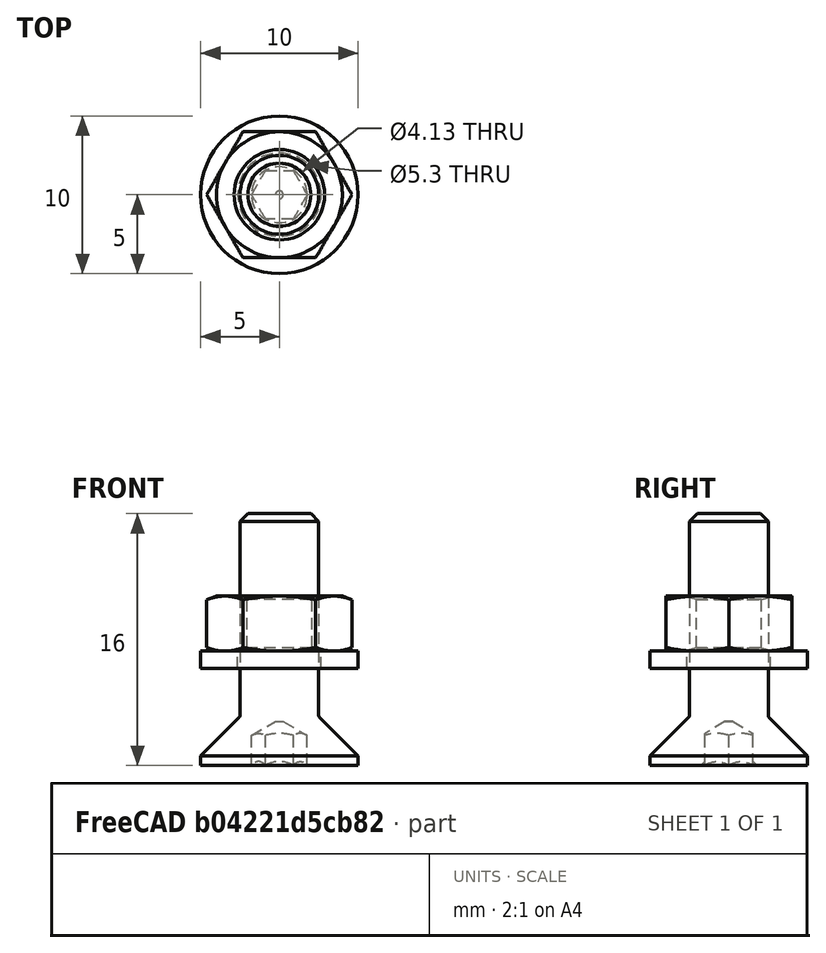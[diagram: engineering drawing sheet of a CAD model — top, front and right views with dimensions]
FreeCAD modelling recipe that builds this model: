
FCSTD DOCUMENT  (FreeCAD 0.20R29177 +426 (Git))
Label: ASM_GantrySkate
License: All rights reserved
LicenseURL: http://en.wikipedia.org/wiki/All_rights_reserved
objects: Part::FeaturePython×6, App::Link×5, App::DocumentObjectGroup×4, PartDesign::CoordinateSystem×1, App::FeaturePython×1, App::Part×1
note: 7 computed .brp shape members not serialized (recipe doc carries the construction recipe); baked Part::Feature solids carry a one-line shape summary decoded from their .brp
EXTERNAL_REF file=GantryBracket.FCStd obj=LCS_Origin
EXTERNAL_REF file=GantryBracket.FCStd obj=Assembly
EXTERNAL_REF file=GantryBracket.FCStd obj=LCS_wheel1
EXTERNAL_REF file=GantryWheel.FCStd obj=LCS_Origin
EXTERNAL_REF file=GantryWheel.FCStd obj=Assembly
EXTERNAL_REF file=GantryBracket.FCStd obj=LCS_wheel2
EXTERNAL_REF file=GantryBracket.FCStd obj=LCS_wheel3
EXTERNAL_REF file=GantryBracket.FCStd obj=LCS_wheel4
EXTERNAL_REF file=Params.FCStd obj=Spreadsheet
EXTERNAL_REF file=GantryBracket.FCStd obj=Sketch
EXTERNAL_REF file=GantryBracket.FCStd obj=Pad

FEATURE [App::DocumentObjectGroup] Parts
FEATURE [PartDesign::CoordinateSystem] LCS_Origin
  AttacherType = Attacher::AttachEngine3D
  MapMode = 2
  Support = -> [X_Axis]
FEATURE [App::FeaturePython] Variables  # WARN: FeaturePython — macro-defined, semantics opaque (R4)
  Type = App::PropertyContainer
FEATURE [App::DocumentObjectGroup] Constraints
FEATURE [App::DocumentObjectGroup] Configurations
FEATURE [App::Link] GantryBracket
  AttachedBy = #LCS_Origin
  AttachedTo = Parent Assembly#LCS_Origin
  LinkedObject = -> <external GantryBracket.FCStd>#Assembly
  SolverId = Asm4EE
  expr: Placement = LCS_Origin.Placement * AttachmentOffset * GantryBracket#LCS_Origin.Placement ^ -1
FEATURE [App::Link] GantryWheel
  AttachedBy = #LCS_Origin
  AttachedTo = GantryBracket#LCS_wheel1
  LinkPlacement = pos=(-19.85,20,3) rot=(0,0,1;1.5708rad)
  LinkedObject = -> <external GantryWheel.FCStd>#Assembly
  Placement = pos=(-19.85,20,3) rot=(0,0,1;1.5708rad)
  SolverId = Asm4EE
  expr: Placement = GantryBracket.Placement * GantryBracket#LCS_wheel1.Placement * AttachmentOffset * GantryWheel#LCS_Origin.Placement ^ -1
FEATURE [App::Link] GantryWheel001
  AttachedBy = #LCS_Origin
  AttachedTo = GantryBracket#LCS_wheel2
  LinkPlacement = pos=(19.85,20,3) rot=(0,0,1;1.5708rad)
  LinkedObject = -> <external GantryWheel.FCStd>#Assembly
  Placement = pos=(19.85,20,3) rot=(0,0,1;1.5708rad)
  SolverId = Asm4EE
  expr: Placement = GantryBracket.Placement * GantryBracket#LCS_wheel2.Placement * AttachmentOffset * GantryWheel#LCS_Origin.Placement ^ -1
FEATURE [App::Link] GantryWheel002
  AttachedBy = #LCS_Origin
  AttachedTo = GantryBracket#LCS_wheel3
  LinkPlacement = pos=(-19.85,-20,3) rot=(0,0,1;1.5708rad)
  LinkedObject = -> <external GantryWheel.FCStd>#Assembly
  Placement = pos=(-19.85,-20,3) rot=(0,0,1;1.5708rad)
  SolverId = Asm4EE
  expr: Placement = GantryBracket.Placement * GantryBracket#LCS_wheel3.Placement * AttachmentOffset * GantryWheel#LCS_Origin.Placement ^ -1
FEATURE [App::Link] GantryWheel003
  AttachedBy = #LCS_Origin
  AttachedTo = GantryBracket#LCS_wheel4
  LinkPlacement = pos=(19.85,-20,3) rot=(0,0,1;1.5708rad)
  LinkedObject = -> <external GantryWheel.FCStd>#Assembly
  Placement = pos=(19.85,-20,3) rot=(0,0,1;1.5708rad)
  SolverId = Asm4EE
  expr: Placement = GantryBracket.Placement * GantryBracket#LCS_wheel4.Placement * AttachmentOffset * GantryWheel#LCS_Origin.Placement ^ -1
FEATURE [Part::FeaturePython] Screw  label="M5x16-Screw"  # Fasteners workbench fastener (typed FeaturePython)
  Placement = pos=(19.85,0,-3.156) rot=(1,0,0;3.14159rad)
  baseObject = -> <external GantryBracket.FCStd>#Sketch [Edge23]
  diameter = 5
  invert = true
  leftHanded = false
  length = 3
  lengthCustom = 16
  matchOuter = false
  offset = 3.156
  thread = false
  type = 18
  expr: offset = <<Params>>#<<Params>>.SheetMetalThickness * 1mm + 0.5mm
FEATURE [Part::FeaturePython] Washer  label="M5-Washer"  # Fasteners workbench fastener (typed FeaturePython)
  Placement = pos=(19.85,0,3) rot=(0,0,1;0rad)
  baseObject = -> <external GantryBracket.FCStd>#Sketch [Edge23]
  diameter = 6
  invert = false
  matchOuter = false
  offset = 3
  type = 3
  expr: offset = <<GantryBracket>>#<<Pad>>.Length
FEATURE [Part::FeaturePython] Nut  label="M5-Nut"  # Fasteners workbench fastener (typed FeaturePython)
  Placement = pos=(19.85,0,4.1) rot=(0,0,1;0rad)
  baseObject = -> Washer [Edge1]
  diameter = 7
  invert = false
  leftHanded = false
  matchOuter = false
  offset = 0
  thread = false
  type = 7
FEATURE [Part::FeaturePython] Array_Screw  label="Array_M5x12-Screw"  # Draft array (typed FeaturePython)
  ArraySteps = 0
  ArrayType = Circular Array
  Axis = LCS_Origin.Z
  Count = 2
  ElementCount = 2
  FullAngle = 360
  IntervalAngle = 180
  LinearSteps = 0
  PlacementList = 2 placements: [(19.85,0,-3.156),(-19.85,2.43092e-15,-3.156)]
  ScaleList = (2) [(1,1,1),(1,1,1)]
  ShowElement = false
  SourceObject = -> Screw
FEATURE [Part::FeaturePython] Array_Washer  label="Array_M5-Washer"  # Draft array (typed FeaturePython)
  ArraySteps = 0
  ArrayType = Circular Array
  Axis = LCS_Origin.Z
  Count = 2
  ElementCount = 2
  FullAngle = 360
  IntervalAngle = 180
  LinearSteps = 0
  PlacementList = 2 placements: [(19.85,0,3),(-19.85,2.43092e-15,3)]
  ScaleList = (2) [(1,1,1),(1,1,1)]
  ShowElement = false
  SourceObject = -> Washer
FEATURE [Part::FeaturePython] Array_Nut  label="Array_M5-Nut"  # Draft array (typed FeaturePython)
  ArraySteps = 0
  ArrayType = Circular Array
  Axis = LCS_Origin.Z
  Count = 2
  ElementCount = 2
  FullAngle = 360
  IntervalAngle = 180
  LinearSteps = 0
  PlacementList = 2 placements: [(19.85,0,4.1),(-19.85,2.43092e-15,4.1)]
  ScaleList = (2) [(1,1,1),(1,1,1)]
  ShowElement = false
  SourceObject = -> Nut
FEATURE [App::DocumentObjectGroup] Fasteners
  Group = -> [Screw,Washer,Nut,Array_Screw,Array_Washer,Array_Nut]
FEATURE [App::Part] Assembly
  AssemblyType = Part::Link
  Group = -> [LCS_Origin,Variables,Constraints,Configurations,GantryBracket,GantryWheel,GantryWheel001,GantryWheel002,GantryWheel003,Fasteners,Screw,Array_Screw,Washer,Array_Washer,Nut,Array_Nut]
  Origin = -> Origin
  Type = Assembly

RESOLVED EXTERNAL PARTS (link-assembly join: the EXTERNAL_REF files above that resolve inside this repo's crawl, each included once):
---- part GantryBracket.FCStd = doc fcstd_fd0a777b0641 ----
FCSTD DOCUMENT  (FreeCAD 0.20R29177 +426 (Git))
Label: GantryBracket
License: All rights reserved
LicenseURL: http://en.wikipedia.org/wiki/All_rights_reserved
objects: PartDesign::CoordinateSystem×5, App::DocumentObjectGroup×3, App::FeaturePython×1, Sketcher::SketchObject×1, PartDesign::Pad×1, PartDesign::Body×1, App::Part×1
note: 9 computed .brp shape members not serialized (recipe doc carries the construction recipe); baked Part::Feature solids carry a one-line shape summary decoded from their .brp

FEATURE [App::DocumentObjectGroup] Parts
FEATURE [PartDesign::CoordinateSystem] LCS_Origin
  AttacherType = Attacher::AttachEngine3D
  MapMode = 2
  Support = -> [X_Axis]
FEATURE [App::FeaturePython] Variables  # WARN: FeaturePython — macro-defined, semantics opaque (R4)
  Type = App::PropertyContainer
FEATURE [App::DocumentObjectGroup] Constraints
FEATURE [App::DocumentObjectGroup] Configurations
FEATURE [Sketcher::SketchObject] Sketch
  FullyConstrained = true
  MapMode = 5
  Support = -> [XY_Plane001]
  sketch-geometry (29):
    g0: ArcOfCircle CenterX=-29.75 CenterY=29.75 CenterZ=0 NormalX=0 NormalY=0 NormalZ=1 AngleXU=0 Radius=3 StartAngle=1.5708 EndAngle=3.14159
    g1: LineSegment StartX=-29.75 StartY=32.75 StartZ=0 EndX=29.75 EndY=32.75 EndZ=0
    g2: ArcOfCircle CenterX=29.75 CenterY=29.75 CenterZ=0 NormalX=0 NormalY=0 NormalZ=1 AngleXU=0 Radius=3 StartAngle=5e-16 EndAngle=1.5708
    g3: LineSegment StartX=32.75 StartY=29.75 StartZ=0 EndX=32.75 EndY=-29.75 EndZ=0
    g4: ArcOfCircle CenterX=29.75 CenterY=-29.75 CenterZ=0 NormalX=0 NormalY=0 NormalZ=1 AngleXU=0 Radius=3 StartAngle=4.71239 EndAngle=6.28319
    g5: LineSegment StartX=29.75 StartY=-32.75 StartZ=0 EndX=-29.75 EndY=-32.75 EndZ=0
    g6: ArcOfCircle CenterX=-29.75 CenterY=-29.75 CenterZ=0 NormalX=0 NormalY=0 NormalZ=1 AngleXU=0 Radius=3 StartAngle=3.14159 EndAngle=4.71239
    g7: LineSegment StartX=-32.75 StartY=-29.75 StartZ=0 EndX=-32.75 EndY=29.75 EndZ=0
    g8: GeomPoint X=-32.75 Y=32.75 Z=0
    g9: GeomPoint X=32.75 Y=-32.75 Z=0
    g10: Circle CenterX=0 CenterY=0 CenterZ=0 NormalX=0 NormalY=0 NormalZ=1 AngleXU=0 Radius=2.55
    g11: Circle CenterX=-19.85 CenterY=-20 CenterZ=0 NormalX=0 NormalY=0 NormalZ=1 AngleXU=0 Radius=3.6
    g12: Circle CenterX=19.85 CenterY=-20 CenterZ=0 NormalX=0 NormalY=0 NormalZ=1 AngleXU=0 Radius=3.6
    g13: Circle CenterX=19.85 CenterY=20 CenterZ=0 NormalX=0 NormalY=0 NormalZ=1 AngleXU=0 Radius=3.6
    g14: Circle CenterX=-19.85 CenterY=20 CenterZ=0 NormalX=0 NormalY=0 NormalZ=1 AngleXU=0 Radius=3.6
    g15: LineSegment StartX=-19.85 StartY=20 StartZ=0 EndX=19.85 EndY=20 EndZ=0
    g16: LineSegment StartX=19.85 StartY=20 StartZ=0 EndX=19.85 EndY=-20 EndZ=0
    g17: ArcOfCircle CenterX=-10 CenterY=-20 CenterZ=0 NormalX=0 NormalY=0 NormalZ=1 AngleXU=0 Radius=2.5 StartAngle=1.5708 EndAngle=4.71239
    g18: ArcOfCircle CenterX=10 CenterY=-20 CenterZ=0 NormalX=0 NormalY=0 NormalZ=1 AngleXU=0 Radius=2.5 StartAngle=4.71239 EndAngle=7.85398
    g19: LineSegment StartX=-10 StartY=-22.5 StartZ=0 EndX=10 EndY=-22.5 EndZ=0
    g20: LineSegment StartX=10 StartY=-17.5 StartZ=0 EndX=-10 EndY=-17.5 EndZ=0
    g21: ArcOfCircle CenterX=-10 CenterY=20 CenterZ=0 NormalX=0 NormalY=0 NormalZ=1 AngleXU=0 Radius=2.5 StartAngle=1.5708 EndAngle=4.71239
    g22: ArcOfCircle CenterX=10 CenterY=20 CenterZ=0 NormalX=0 NormalY=0 NormalZ=1 AngleXU=0 Radius=2.5 StartAngle=4.71239 EndAngle=7.85398
    g23: LineSegment StartX=-10 StartY=17.5 StartZ=0 EndX=10 EndY=17.5 EndZ=0
    g24: LineSegment StartX=10 StartY=22.5 StartZ=0 EndX=-10 EndY=22.5 EndZ=0
    g25: LineSegment StartX=10 StartY=17.5 StartZ=0 EndX=10 EndY=-17.5 EndZ=0
    g26: LineSegment StartX=-19.85 StartY=20 StartZ=0 EndX=-19.85 EndY=0 EndZ=0
    g27: Circle CenterX=-19.85 CenterY=0 CenterZ=0 NormalX=0 NormalY=0 NormalZ=1 AngleXU=0 Radius=2.55
    g28: Circle CenterX=19.85 CenterY=0 CenterZ=0 NormalX=0 NormalY=0 NormalZ=1 AngleXU=0 Radius=3.6
  constraints (69):
    c: Tangent(g0,g1) = 1.5708
    c: Tangent(g1,g2) = 1.5708
    c: Tangent(g2,g3) = 1.5708
    c: Tangent(g3,g4) = 1.5708
    c: Tangent(g4,g5) = 1.5708
    c: Tangent(g5,g6) = 1.5708
    c: Tangent(g6,g7) = 1.5708
    c: Tangent(g7,g0) = 1.5708
    c: Horizontal(g1)
    c: Horizontal(g5)
    c: Vertical(g3)
    c: Vertical(g7)
    c: Equal(g0,g2)
    c: Equal(g2,g4)
    c: Equal(g4,g6)
    c: PointOnObject(g8,g1)
    c: PointOnObject(g8,g7)
    c: PointOnObject(g9,g3)
    c: PointOnObject(g9,g5)
    c: Symmetric(g2,g6,g-1)
    c: DistanceY(g4,g1) = 65.5
    c: Equal(g1,g3)
    c: Radius(g2) = 3
    c: Coincident(g10,g-1)
    c: Equal(g11,g12)
    c: Equal(g12,g13)
    c: Equal(g13,g14)
    c: Coincident(g15,g14)
    c: Coincident(g15,g13)
    c: Coincident(g16,g13)
    c: Coincident(g16,g12)
    c: Vertical(g16)
    c: Horizontal(g15)
    c: Symmetric(g13,g11,g10)
    c: Symmetric(g12,g14,g10)
    c: DistanceY(g14,g0) = 12.75
    c: DistanceX(g0,g14) = 12.9
    c: Diameter(g13) = 7.2
    c: Diameter(g10) = 5.1
    c: Tangent(g17,g19) = -1.5708
    c: Tangent(g19,g18) = -1.5708
    c: Tangent(g18,g20) = -1.5708
    c: Tangent(g20,g17) = -1.5708
    c: Equal(g17,g18)
    c: Horizontal(g19)
    c: Tangent(g21,g23) = -1.5708
    c: Tangent(g23,g22) = -1.5708
    c: Tangent(g22,g24) = -1.5708
    c: Tangent(g24,g21) = -1.5708
    c: Equal(g21,g22)
    c: Equal(g22,g18)
    c: Equal(g20,g23)
    c: Diameter(g22) = 5
    c: Symmetric(g18,g21,g10)
    c: Horizontal(g23)
    c: PointOnObject(g22,g15)
    c: Coincident(g25,g22)
    c: Coincident(g25,g18)
    c: Vertical(g25)
    c: DistanceX(g24,g24) = 20
    c: Coincident(g26,g14)
    c: PointOnObject(g26,g-1)
    c: Vertical(g26)
    c: Coincident(g27,g26)
    c: PointOnObject(g28,g16)
    c: PointOnObject(g28,g-1)
    c: Equal(g28,g13)
    c: Equal(g27,g10)
    c: DistanceX(g27,g28) = 39.7  'HoleSpacing'
FEATURE [PartDesign::Pad] Pad
  Direction = (0,0,1)
  Length = 3
  Length2 = 10
  Profile = -> Sketch
  ReferenceAxis = -> Sketch [N_Axis]
  Type = 0
FEATURE [PartDesign::Body] Body
  Group = -> [Sketch,Pad]
  Origin = -> Origin001
  Tip = -> Pad
FEATURE [PartDesign::CoordinateSystem] LCS_wheel1
  AttacherType = Attacher::AttachEngine3D
  MapMode = 11
  Placement = pos=(-19.85,20,3) rot=(0,0,1;1.5708rad)
  Support = -> [Pad]
FEATURE [PartDesign::CoordinateSystem] LCS_wheel2
  AttacherType = Attacher::AttachEngine3D
  MapMode = 11
  Placement = pos=(19.85,20,3) rot=(0,0,1;1.5708rad)
  Support = -> [Pad]
FEATURE [PartDesign::CoordinateSystem] LCS_wheel3
  AttacherType = Attacher::AttachEngine3D
  MapMode = 11
  Placement = pos=(-19.85,-20,3) rot=(0,0,1;1.5708rad)
  Support = -> [Pad]
FEATURE [PartDesign::CoordinateSystem] LCS_wheel4
  AttacherType = Attacher::AttachEngine3D
  MapMode = 11
  Placement = pos=(19.85,-20,3) rot=(0,0,1;1.5708rad)
  Support = -> [Pad]
FEATURE [App::Part] Assembly
  AssemblyType = Part::Link
  Group = -> [LCS_Origin,Variables,Constraints,Configurations,Body,LCS_wheel1,LCS_wheel2,LCS_wheel3,LCS_wheel4]
  Origin = -> Origin
  Type = Assembly
---- part GantryWheel.FCStd = doc fcstd_9ffe28085d5b ----
FCSTD DOCUMENT  (FreeCAD 0.20R29177 +426 (Git))
Label: GantryWheel
License: All rights reserved
LicenseURL: http://en.wikipedia.org/wiki/All_rights_reserved
objects: App::DocumentObjectGroup×3, PartDesign::CoordinateSystem×1, App::FeaturePython×1, Sketcher::SketchObject×1, PartDesign::Revolution×1, PartDesign::Body×1, App::Part×1
note: 5 computed .brp shape members not serialized (recipe doc carries the construction recipe); baked Part::Feature solids carry a one-line shape summary decoded from their .brp

FEATURE [App::DocumentObjectGroup] Parts
FEATURE [PartDesign::CoordinateSystem] LCS_Origin
  AttacherType = Attacher::AttachEngine3D
  MapMode = 2
  Support = -> [X_Axis]
FEATURE [App::FeaturePython] Variables  # WARN: FeaturePython — macro-defined, semantics opaque (R4)
  Type = App::PropertyContainer
FEATURE [App::DocumentObjectGroup] Constraints
FEATURE [App::DocumentObjectGroup] Configurations
FEATURE [Sketcher::SketchObject] Sketch
  FullyConstrained = true
  MapMode = 5
  Placement = pos=(0,0,0) rot=(1,0,0;1.5708rad)
  Support = -> [XZ_Plane001]
  sketch-geometry (11):
    g0: LineSegment StartX=0 StartY=19.9213 StartZ=0 EndX=3 EndY=19.9213 EndZ=0
    g1: LineSegment StartX=3 StartY=19.9213 StartZ=0 EndX=5.12132 EndY=17.8 EndZ=0
    g2: LineSegment StartX=5.12132 StartY=17.8 StartZ=0 EndX=5.12132 EndY=14.8 EndZ=0
    g3: LineSegment StartX=5.12132 StartY=14.8 StartZ=0 EndX=10.1 EndY=14.8 EndZ=0
    g4: LineSegment StartX=10.1 StartY=14.8 StartZ=0 EndX=11.5 EndY=13.4 EndZ=0
    g5: LineSegment StartX=11.5 StartY=13.4 StartZ=0 EndX=11.5 EndY=7.4 EndZ=0
    g6: LineSegment StartX=11.5 StartY=7.4 StartZ=0 EndX=10.1 EndY=6 EndZ=0
    g7: LineSegment StartX=10.1 StartY=6 StartZ=0 EndX=5 EndY=6 EndZ=0
    g8: LineSegment StartX=5 StartY=6 StartZ=0 EndX=5 EndY=0 EndZ=0
    g9: LineSegment StartX=5 StartY=0 StartZ=0 EndX=0 EndY=0 EndZ=0
    g10: LineSegment StartX=0 StartY=0 StartZ=0 EndX=0 EndY=19.9213 EndZ=0
  constraints (32):
    c: PointOnObject(g0,g-2)
    c: Horizontal(g0)
    c: Coincident(g0,g1)
    c: Coincident(g1,g2)
    c: Vertical(g2)
    c: Coincident(g2,g3)
    c: Horizontal(g3)
    c: Coincident(g3,g4)
    c: Coincident(g4,g5)
    c: Vertical(g5)
    c: Coincident(g5,g6)
    c: Coincident(g6,g7)
    c: Horizontal(g7)
    c: Coincident(g7,g8)
    c: Vertical(g8)
    c: PointOnObject(g9,g-1)
    c: Coincident(g9,g-1)
    c: Coincident(g9,g10)
    c: Coincident(g10,g0)
    c: Equal(g6,g4)
    c: DistanceY(g5,g5) = 6
    c: Angle(g6,g7) = 2.35619
    c: Angle(g3,g4) = 2.35619
    c: DistanceY(g6,g3) = 8.8
    c: Angle(g1,g2) = 2.35619
    c: Equal(g2,g1)
    c: Equal(g1,g0)
    c: DistanceX(g0,g0) = 3
    c: Coincident(g9,g8)
    c: DistanceY(g8,g8) = 6
    c: DistanceX(g9,g9) = 5
    c: DistanceX(g9,g5) = 11.5
FEATURE [PartDesign::Revolution] Revolution
  Angle = 360
  Axis = (0,-2e-16,1)
  Base = (0,0,0)
  Placement = pos=(0,0,0) rot=(1,0,0;1.5708rad)
  Profile = -> Sketch
  ReferenceAxis = -> Sketch [V_Axis]
  Reversed = true
FEATURE [PartDesign::Body] Body
  Group = -> [Sketch,Revolution]
  Origin = -> Origin001
  Tip = -> Revolution
FEATURE [App::Part] Assembly
  AssemblyType = Part::Link
  Group = -> [LCS_Origin,Variables,Constraints,Configurations,Body]
  Origin = -> Origin
  Type = Assembly
---- part Params.FCStd = doc fcstd_b8f81ed59c9d ----
FCSTD DOCUMENT  (FreeCAD 0.20R29177 +426 (Git))
Label: Params
License: All rights reserved
LicenseURL: http://en.wikipedia.org/wiki/All_rights_reserved
objects: Spreadsheet::Sheet×1

FEATURE [Spreadsheet::Sheet] Spreadsheet  label="Params"
  cells = A1=DriveWheelWidth; B1(DriveWheelWidth)=10; D1=PlywoodThickness; E1(PlywoodThickness)=18.5; A2=DriveWheelMajorDiameter; B2(DriveWheelMajorDiameter)=52; D2=ExtensionArmCenterOffset; E2(ExtensionArmCenterOffset)=23; A3=DriveWheelCrown; B3(DriveWheelCrown)=2; D3=SheetMetalThickness; E3(SheetMetalThickness)=2.656; A4=DriveWheelTireThickness; B4(DriveWheelTireThickness)=3; D4=CeilingPlateDiameter; E4(CeilingPlateDiameter)=463; A6=DriveUnitAngle; B6(DriveUnitAngle)=30; D6=TableRollerMountHoleSpacing; E6(TableRollerMountHoleSpacing)=24; A7=DriveRadius; B7(DriveRadius)=280; D7=TableRollerMountHoleOffset; E7(TableRollerMountHoleOffset)=12; A8=DriveAdjMiddleOffset; B8(DriveAdjMiddleOffset)=90; D8=TableRollerDriveSupportRadius; E8(TableRollerDriveSupportRadius)=218; A9=RotationDriveOffset; B9(RotationDriveOffset)=29; D9=TableRollerSideRadius; E9(TableRollerSideRadius)=164; A10=FrontSkateOffset; B10(FrontSkateOffset)=350; D10=TableRollerDriveSupportAngle; E10(TableRollerDriveSupportAngle)=13.5; A11=RearSkateOffset; B11(RearSkateOffset)=150; D11=TableRollerSideAngle; E11(TableRollerSideAngle)=20; A13=CablePulleyDiameter; B13(CablePulleyDiameter)=120; D13=RoomWidth; E13(RoomWidth)=3650; D14=RoomLength; E14(RoomLength)=3650; A15=ExtensionDriverOffsetX; B15(ExtensionDriverOffsetX)=100; D15=RoomHeight; E15(RoomHeight)=2440; A16=ExtensionDriverOffsetY; B16(ExtensionDriverOffsetY)=-36
